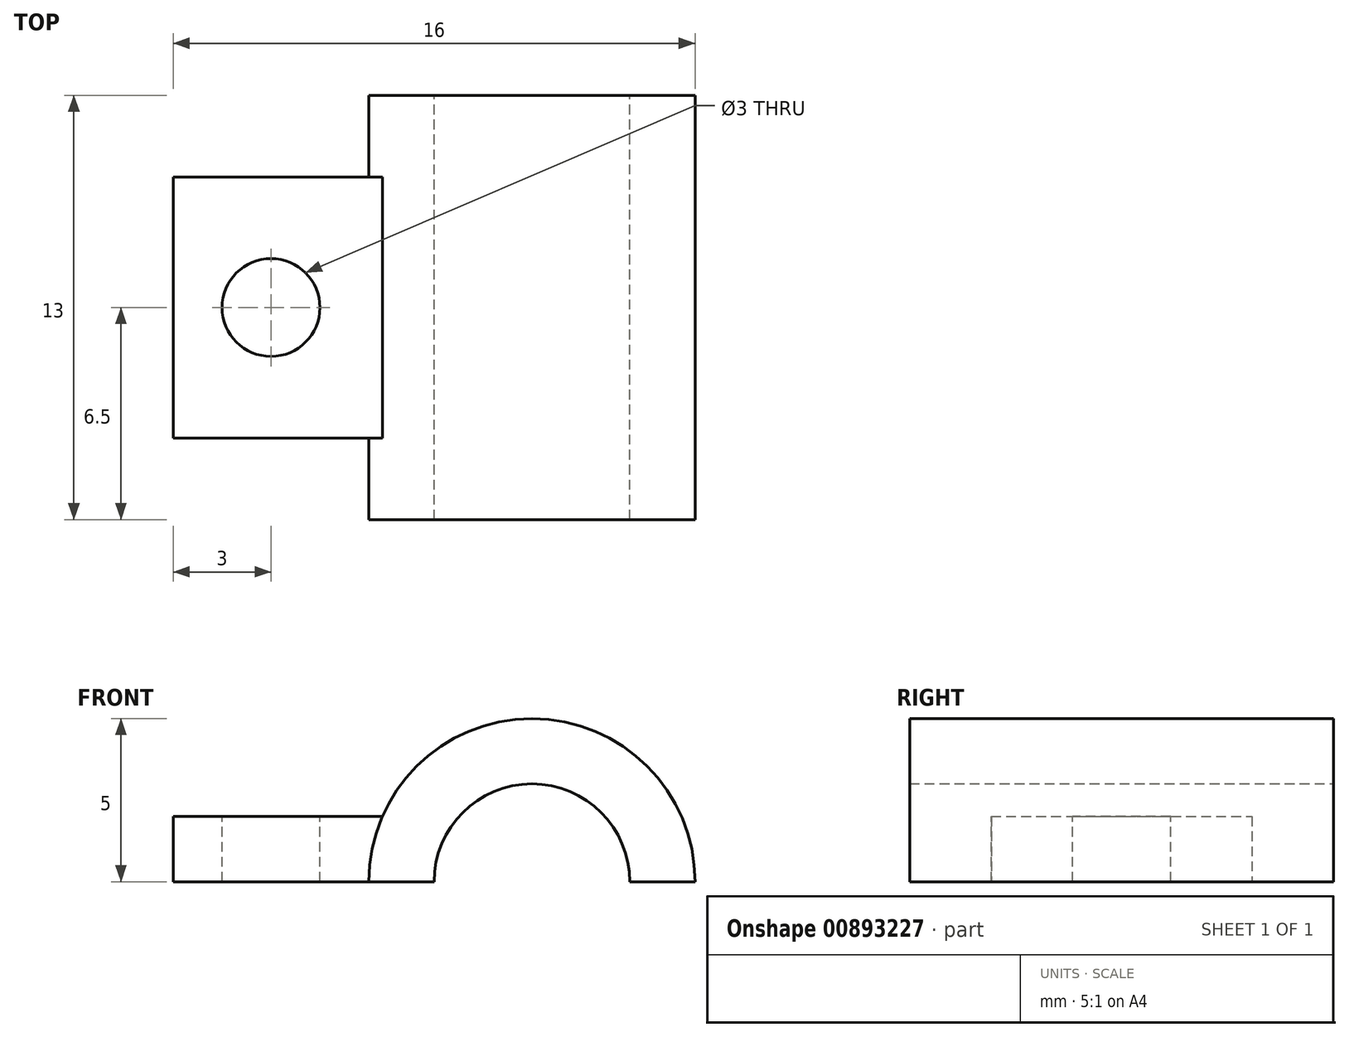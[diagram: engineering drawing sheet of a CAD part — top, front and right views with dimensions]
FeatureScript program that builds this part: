
annotation { "Feature Type Name" : "Feature", "Feature Type Description" : "" }
export const myFeature = defineFeature(function(context is Context, id is Id, definition is map)
    precondition{}
    {
        {
            var Q0;
            Q0=qCreatedBy(makeId("Front.planeOp"),FACE);
            var sketch = newSketch(context, id + "F0", { "sketchPlane" : qUnion([Q0])});
            skArc(sketch, "E0", {"start": v(5, 0) * mm, "mid": v(0, 5) * mm, "end": v(-5, 0) * mm});
            skArc(sketch, "E1", {"start": v(3, 0) * mm, "mid": v(0, 3) * mm, "end": v(-3, 0) * mm});
            skLineSegment(sketch, "E2", {"start": v(-5, 0) * mm, "end": v(-3, 0) * mm});
            skLineSegment(sketch, "E3", {"start": v(3, 0) * mm, "end": v(5, 0) * mm});
            skSolve(sketch);
        }
        {
            var Q0;
            Q0 = qSketchRegion(id + "F0", true);
            extrude(context, id + "F1", {"entities" : qUnion([Q0]), "endBound" : BoundingType.SYMMETRIC, "depth" : 13 * mm, "offsetDistance" : 25 * mm});
        }
        {
            var Q0;
            Q0=qCreatedBy(makeId("Top.planeOp"),FACE);
            var sketch = newSketch(context, id + "F2", { "sketchPlane" : qUnion([Q0])});
            skLineSegment(sketch, "E4", {"start": v(-11, 4) * mm, "end": v(-11, -4) * mm});
            skLineSegment(sketch, "E5", {"start": v(-11, -4) * mm, "end": v(-3, -4) * mm});
            skLineSegment(sketch, "E6", {"start": v(-3, -4) * mm, "end": v(-3, 4) * mm});
            skLineSegment(sketch, "E7", {"start": v(-3, 4) * mm, "end": v(-11, 4) * mm});
            skSolve(sketch);
        }
        {
            var Q0;
            Q0 = qSketchRegion(id + "F2", true);
            extrude(context, id + "F3", {"entities" : qUnion([Q0]), "operationType" : NewBodyOperationType.ADD, "depth" : 2 * mm, "offsetDistance" : 25 * mm});
        }
        {
            var Q0;
            Q0=makeQuery(id+"F3.opExtrude","CAP_FACE",FACE,{"disambiguationData":[OSD([sQuery(id+"F2.wireOp",EDGE,"E4"),sQuery(id+"F2.wireOp",EDGE,"E5"),sQuery(id+"F2.wireOp",EDGE,"E6"),sQuery(id+"F2.wireOp",EDGE,"E7")])],"isStart":false});
            var sketch = newSketch(context, id + "F4", { "sketchPlane" : qUnion([Q0])});
            skCircle(sketch, "E8", {"center": v(-8, 0) * mm, "radius": 1.5 * mm});
            skSolve(sketch);
        }
        {
            var Q0;
            Q0 = qSketchRegion(id + "F4", true);
            extrude(context, id + "F5", {"entities" : qUnion([Q0]), "operationType" : NewBodyOperationType.REMOVE, "oppositeDirection" : true, "depth" : 25 * mm, "offsetDistance" : 25 * mm});
        }
    });
